# Revit family: окна.rehau_двупольное
name_source: partatom
category: Окна
revit_build: Autodesk Revit 2017 (Build: 20170816_0615(x64)
units: mm (PartAtom-declared; Revit-internal decimal feet)

## family parameters
Всегда вертикально = Да
Заголовок OmniClass = Windows
Номер OmniClass = 23.30.20.00
Общий = Нет
Основа = Стена
При загрузке вырезать с полостями = Нет
Точка расчета площади = Нет

## types (2) — shared parameters
24 газ = сп : однокамерный (24мм) заполнение газом
24 обычный = сп : однокамерный (24мм) обычный
24 энерго = сп : однокамерный (24мм) энергосберегающие стекла
32 газ = сп : двухкамерный (32мм) заполнение газом
32 обычный = сп : двухкамерный (32мм) обычный
32 триплекс = сп : двухкамерный (32мм) триплекс
32 энерго = сп : двухкамерный (32мм) энергосберегающие стекла
ADSK_Обозначение = ГОСТ 30674-99
URL = https://www.rehau.com
blitz new = Rehau : BLITZ NEW
delight 78 = Rehau : DELIGHT
euro 64 = Rehau : EURO (коробка 64, импост 78, створка 60)
euro 68 = Rehau : EURO (коробка 68, импост 78, створка 60)
euro 76 = Rehau : EURO (коробка 76, импост 86, створка 74)
grazio 55 = Rehau : GRAZIO (коробка 55)
grazio 63 = Rehau : GRAZIO (коробка 63)
Аналитическая конструкция = Окна с одинарным остеклением - для жилых зданий
Высота подоконника по умолчанию = 900 мм
Группа модели = ОП
Замыкание стены = По основе
Изготовитель = Rehau
Изображение типоразмера = <Нет>
Коэффициент теплопередачи (U) = 5.7361 Вт/(м²·K)
Коэффициент теплопритока от солнечного излучения = 0.86
Материал коробки = <По категории>
Материал отлива = <По категории>
Материал подоконника = <По категории>
Материал стекла = <По категории>
Описание = проем.окно
Примерная высота = 1460 мм
Примерная ширина = 1460 мм
Пропускание видимого света = 0.9
Равные створки = Да
Створка справа = 600 мм
Термостойкость = 0.1743 (м²·K)/Вт
Тип створки слева = створка : глухая
глухая_створка = створка : глухая
обозначение_проема_высота = 243 мм
обозначение_проема_ширина = 243 мм
створка_справа_размер = 730 мм
таблица выбора = каталог профилей Rehau

## per-type parameters (varying)
| type | Тип створки справа |
| 1460х1460 (створка и глухое) | створка : левая |
| 1460х1460 (глухое) | створка : глухая |
